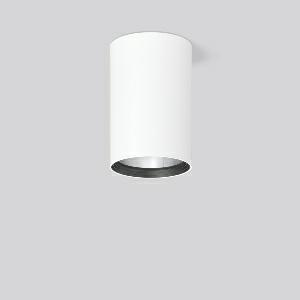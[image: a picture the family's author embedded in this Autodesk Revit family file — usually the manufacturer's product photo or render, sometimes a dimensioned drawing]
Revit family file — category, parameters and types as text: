
# Revit family: heledon_maxi_a_931226_002_1_d017
name_source: partatom
category: Lighting Fixtures
units: mm (PartAtom-declared; Revit-internal decimal feet)

## family parameters
Cut with Voids When Loaded = No
Host = Face
Light Source = No
Part Type = Normal
Room Calculation Point = No
Round Connector Dimension = Use Diameter
Shared = No

## types (1)
- HELEDON maxi A (1 x LED Modul 940, 4400 lm, 4000)
    Apparent Load = 35 VA
    Approval mark = CE
    CIE Flux Codes = 97 100 100 100 100
    Color Rendering = 92
    Color Temperature = 4000
    Default Elevation = 1800 mm
    Description = Series: HELEDON maxi
Cylindrical surface-mounted downlight. Housing: die-cast aluminium, powder-coated. Internal ceiling frame polycarbonate with bayonet mounting. Black plastic ring and recessed LED to prevent glare from the side. Optical assembly with reflector made of MIRO-Silver with 98% total light reflection for outstanding efficiency - can be changed without tools. Best colour rendering index Ra>90. Suitable for Ceiling mounting. Easy installation with a separate ceiling frame with bayonet mounting and plug connection. Driver integrated. Connected via plug-in connector. High quality converter without flickering and stroboscopic effect. The following accessories can be mounted without use of tools: interchangeable lenses, decorative glasses, honeycomb louvre, clear and frosted diffusers, white interchangeable plastic ring. 
Colour: traffic white, matt (RAL 9016)
Diameter: 123 mm
Height: 183 mm
Lamp: LED
Socket: without socket
Colour temperature: 4000K
Colour rendering index (CRI): 92
System power: 35 W
Rated luminous flux: 4400 lm
Luminous efficiency: 126 lm/W
Control gear: Regulated power supply
Protection class: I
Type of protection: IP 20
    Height = 183 mm
    Lamp = 1 x LED Modul 940
    Lamp Light Flux = 4400 lm
    Lamp count = 1
    Length = 123 mm
    Lifetime = 50000 h
    Luminous efficacy = 126 lm/W
    Manufacturer = RZB
    ModVariant = No
    Model = 931226.002.1
    Mounting Place = Ceiling
    Mounting Type = Surface mounted
    Number of Poles = 1
    OnlyDefault = Yes
    Power Factor = 1
    Product Name = HELEDON maxi A
    Product group = Surface mounted downlights
    ProductGroupID = 302
    Protection Class = Protection class I
    Protection Degree = IP 20
    RLX_Detail_Level = 1
    RLX_Emergency_Light_Flux = 0 lm
    RLX_Emergency_Type = 0
    RLX_Emergency_Type_DB = No
    RlxData = <blob elided: 97073 chars, md5=b321b2de>
    Socket = socket
    Standby Power = 0 W
    System Light Flux = 4400 lm
    System Power = 35 W
    Type Comments = Product without accessories
    Type Image = 931192.002.jpg
    URL = http://relux.com
    VarID = ---
    Voltage = 230 V
    Voltage Range = 220-240 V
    Weight = 0.00 kg
    Width = 0 mm  [stored 0 ft]

note: [stored X ft] marks values corroborated as IEEE doubles in the binary element streams (Revit-internal decimal feet)

## geometry (parser evidence)
native form markers: Blend x4, Sweep x11
no freeform markers — native parametric forms only
